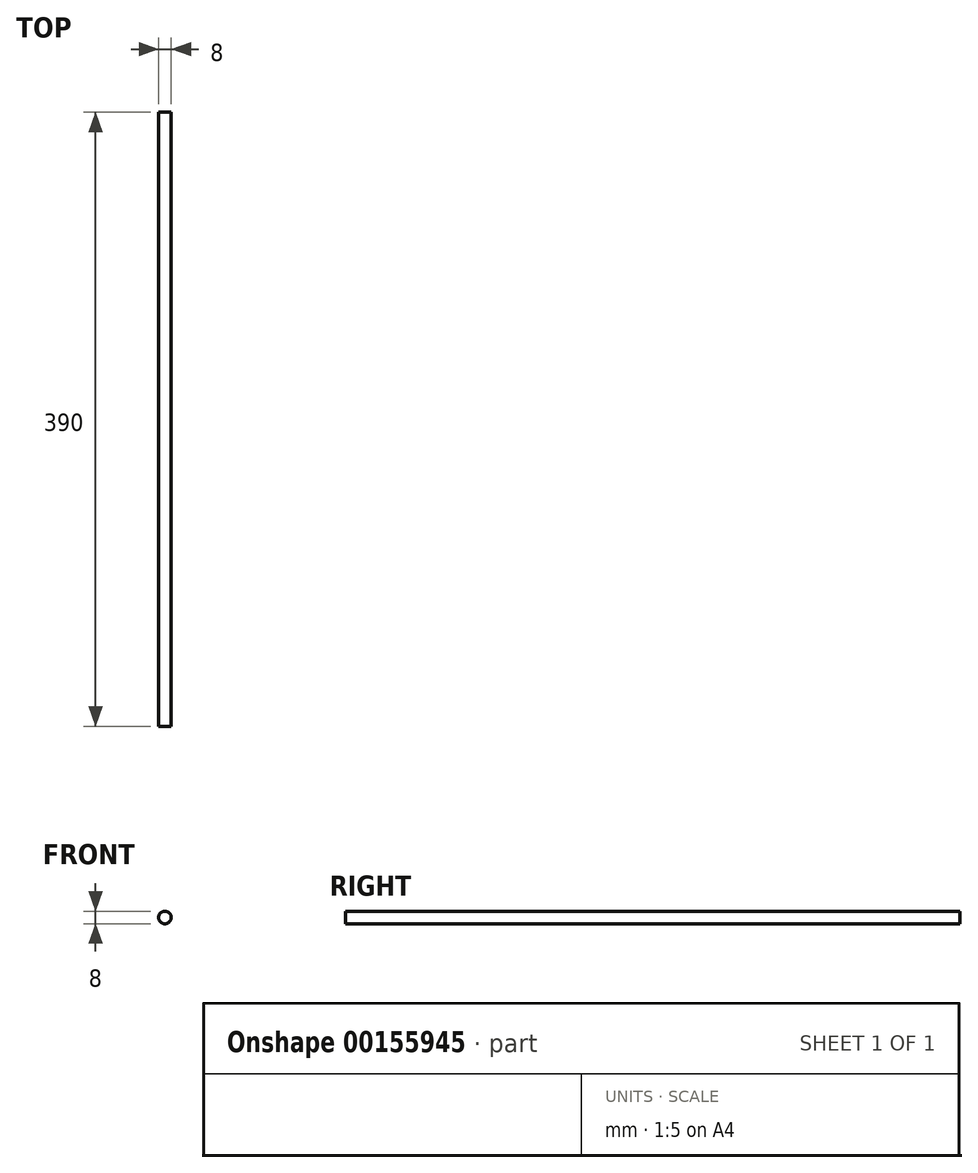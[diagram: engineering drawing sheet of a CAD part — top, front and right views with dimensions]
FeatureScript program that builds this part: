
annotation { "Feature Type Name" : "Feature", "Feature Type Description" : "" }
export const myFeature = defineFeature(function(context is Context, id is Id, definition is map)
    precondition{}
    {
        {
            var Q0;
            Q0=qCreatedBy(makeId("Front.planeOp"),FACE);
            var sketch = newSketch(context, id + "F0", { "sketchPlane" : qUnion([Q0])});
            skCircle(sketch, "E0", {"center": v(-52.62, 47.62) * mm, "radius": 4 * mm});
            skSolve(sketch);
        }
        {
            var Q0;
            Q0=makeQuery(id+"F0.imprint","IMPRINT",FACE,{"disambiguationData":[TD([[makeQuery(id+"F0.imprint","IMPRINT",EDGE,{"derivedFrom":sQuery(id+"F0.wireOp",EDGE,"E0")}),1.0]])]});
            extrude(context, id + "F1", {"entities" : qUnion([Q0]), "oppositeDirection" : true, "depth" : 390 * mm, "offsetDistance" : 25 * mm});
        }
    });
